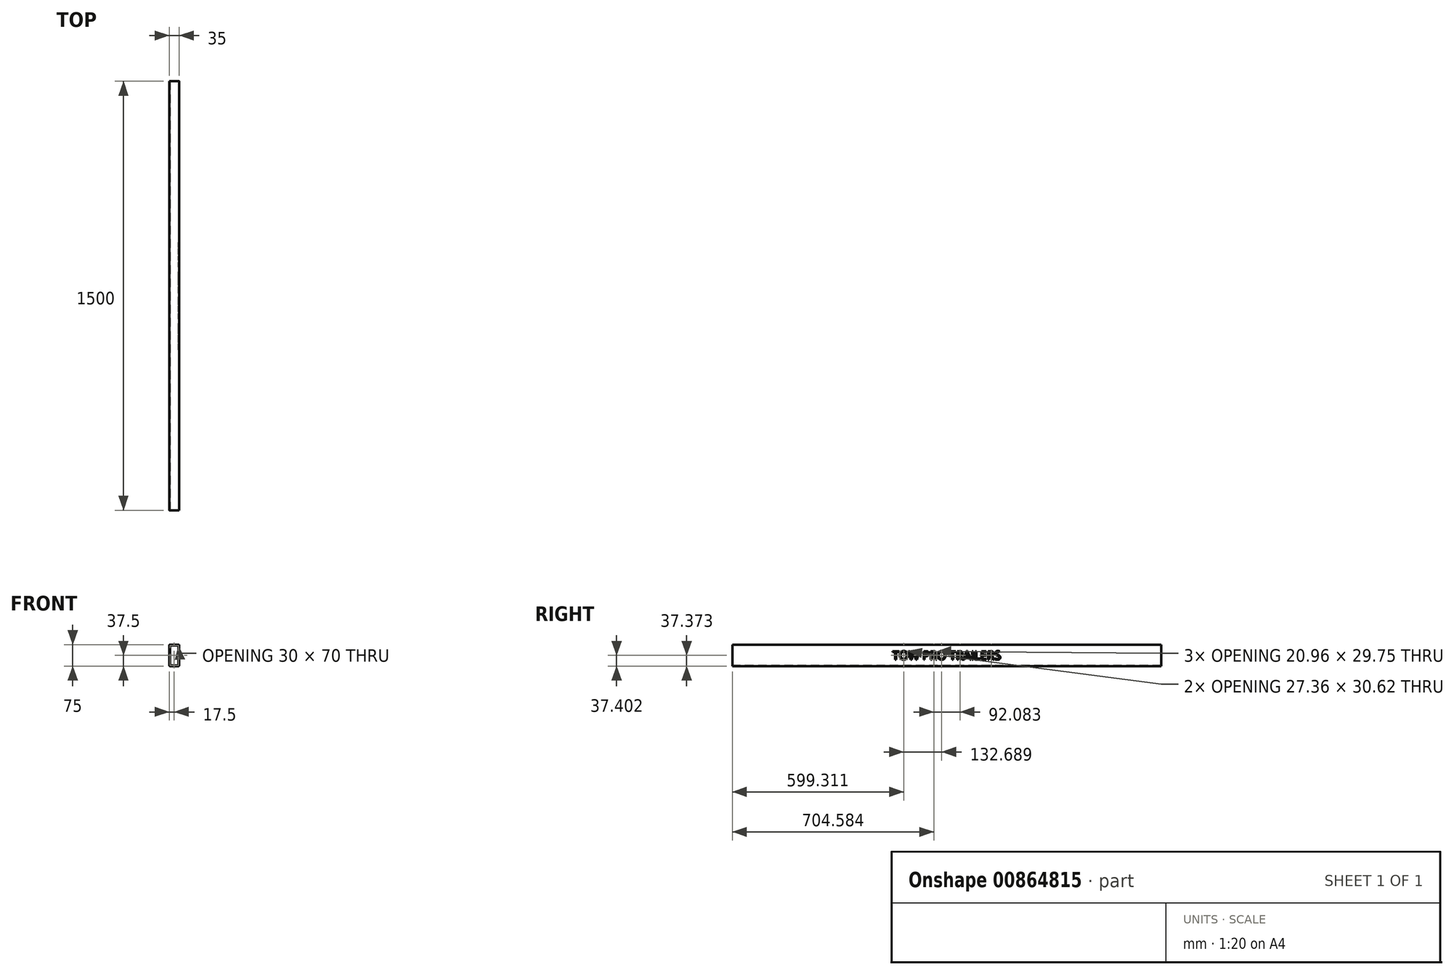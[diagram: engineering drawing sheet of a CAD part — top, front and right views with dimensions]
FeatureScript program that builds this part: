
annotation { "Feature Type Name" : "Feature", "Feature Type Description" : "" }
export const myFeature = defineFeature(function(context is Context, id is Id, definition is map)
    precondition{}
    {
        {
            var Q0;
            Q0=qCreatedBy(makeId("Front.planeOp"),FACE);
            var sketch = newSketch(context, id + "F0", { "sketchPlane" : qUnion([Q0])});
            skLineSegment(sketch, "E0.bottom", {"start": v(14.5, 37.5) * mm, "end": v(-14.5, 37.5) * mm});
            skLineSegment(sketch, "E0.top", {"start": v(14.5, -37.5) * mm, "end": v(-14.5, -37.5) * mm});
            skLineSegment(sketch, "E0.left", {"start": v(17.5, 34.5) * mm, "end": v(17.5, -34.5) * mm});
            skLineSegment(sketch, "E0.right", {"start": v(-17.5, 34.5) * mm, "end": v(-17.5, -34.5) * mm});
            skPoint(sketch, "E0.middle", {"position": v(0, 0) * mm});
            skPoint(sketch, "E1.visualSharp", {"position": v(-17.5, 37.5) * mm});
            skArc(sketch, "E1.filletArc", {"start": v(-14.5, 37.5) * mm, "mid": v(-16.62, 36.62) * mm, "end": v(-17.5, 34.5) * mm});
            skPoint(sketch, "E2.visualSharp", {"position": v(17.5, 37.5) * mm});
            skArc(sketch, "E2.filletArc", {"start": v(17.5, 34.5) * mm, "mid": v(16.62, 36.62) * mm, "end": v(14.5, 37.5) * mm});
            skPoint(sketch, "E3.visualSharp", {"position": v(17.5, -37.5) * mm});
            skArc(sketch, "E3.filletArc", {"start": v(14.5, -37.5) * mm, "mid": v(16.62, -36.62) * mm, "end": v(17.5, -34.5) * mm});
            skPoint(sketch, "E4.visualSharp", {"position": v(-17.5, -37.5) * mm});
            skArc(sketch, "E4.filletArc", {"start": v(-17.5, -34.5) * mm, "mid": v(-16.62, -36.62) * mm, "end": v(-14.5, -37.5) * mm});
            skLineSegment(sketch, "E5.0", {"start": v(15, 34) * mm, "end": v(15, -34) * mm});
            skLineSegment(sketch, "E5.1", {"start": v(14, 35) * mm, "end": v(-14, 35) * mm});
            skLineSegment(sketch, "E5.2", {"start": v(-15, 34) * mm, "end": v(-15, -34) * mm});
            skLineSegment(sketch, "E5.3", {"start": v(14, -35) * mm, "end": v(-14, -35) * mm});
            skPoint(sketch, "E6.visualSharp", {"position": v(-15, 35) * mm});
            skArc(sketch, "E6.filletArc", {"start": v(-14, 35) * mm, "mid": v(-14.7, 34.7) * mm, "end": v(-15, 34) * mm});
            skPoint(sketch, "E7.visualSharp", {"position": v(15, 35) * mm});
            skArc(sketch, "E7.filletArc", {"start": v(15, 34) * mm, "mid": v(14.7, 34.7) * mm, "end": v(14, 35) * mm});
            skPoint(sketch, "E8.visualSharp", {"position": v(-15, -35) * mm});
            skArc(sketch, "E8.filletArc", {"start": v(-15, -34) * mm, "mid": v(-14.7, -34.7) * mm, "end": v(-14, -35) * mm});
            skPoint(sketch, "E9.visualSharp", {"position": v(15, -35) * mm});
            skArc(sketch, "E9.filletArc", {"start": v(14, -35) * mm, "mid": v(14.7, -34.7) * mm, "end": v(15, -34) * mm});
            skSolve(sketch);
        }
        {
            var Q0;
            Q0=makeQuery(id+"F0.imprint","IMPRINT",FACE,{"disambiguationData":[TD([[makeQuery(id+"F0.imprint","IMPRINT",EDGE,{"derivedFrom":sQuery(id+"F0.wireOp",EDGE,"E0.bottom")}),1.0]])]});
            extrude(context, id + "F1", {"entities" : qUnion([Q0]), "oppositeDirection" : true, "depth" : 1500 * mm, "offsetDistance" : 25 * mm});
        }
        {
            var Q0;
            Q0=makeQuery(id+"F1.opExtrude","SWEPT_FACE",FACE,{"disambiguationData":[OSD([sQuery(id+"F0.wireOp",EDGE,"E0.left")])]});
            var sketch = newSketch(context, id + "F2", { "sketchPlane" : qUnion([Q0])});
            skLineSegment(sketch, "E10", {"start": v(0, 0) * mm, "end": v(1500, 0) * mm, "construction": true});
            skText(sketch, "E11", { "text": "TOW PRO TRAILERS", "fontName": "OpenSans-Regular.ttf"});
            skLineSegment(sketch, "E12", {"start": v(750, -34.5) * mm, "end": v(750, 64.21) * mm, "construction": true});
            skPoint(sketch, "E12.endSnap0", {"position": v(750, 34.5) * mm});
            const initialGuessF2  = {"E11": [0.56003, -0.015, 1, 0, 0.03]};
            skSetInitialGuess(sketch, initialGuessF2);
            skSolve(sketch);
        }
        {
            var Q0;
            Q0 = qSketchRegion(id + "F2", true);
            extrude(context, id + "F3", {"entities" : qUnion([Q0]), "operationType" : NewBodyOperationType.REMOVE, "depth" : 25 * mm, "offsetDistance" : 25 * mm, "hasSecondDirection" : true, "secondDirectionOppositeDirection" : true, "secondDirectionDepth" : 25 * mm});
        }
    });
